# Revit family: DA_Клапан_Регулятор_Расхода_КРП_VEOX
name_source: partatom
category: Арматура воздуховодов
units: mm (PartAtom-declared; Revit-internal decimal feet)

## family parameters
Всегда вертикально = Нет
На основе рабочей плоскости = Нет
Номер OmniClass = 23.33.41.17.13
Общий = Нет
При загрузке вырезать с полостями = Нет
Размер круглого соединителя = Использовать диаметр
Тип детали = Вставляется

## types (2) — shared parameters
ADSK_Дата изменения = 13.01.2023
ADSK_Единица измерения = шт.
ADSK_Завод-изготовитель = Veox
ADSK_Количество = 1
ADSK_Марка = КРП
ADSK_Наименование краткое = клапан
CSV = ПР
URL = https://veox.ru
s = 4 мм
КМС = 6.5
Корпус = Оцинкованная сталь
Лопатка = Оцинкованная сталь
Максимальный размер клапана = 600мм
Минимальный размер клапана = 150мм
Фланец = Оцинкованная сталь
Хомут быстросъемный = Да
вылет x2 = 50 мм
тип = 2
zero-valued in all types: Отметка по умолчанию

## per-type parameters (varying)
| type | ИЗОЛЯЦИЯ | Регулятор | сдвиг изоляции |
| КРП  (без изоляции) | Нет | регулятор : 70 | 2 мм |
| КРП  (c изоляцией) | Да | регулятор : 100 | 50 мм |

## geometry (parser evidence)
native form markers: Sweep x2
no freeform markers — native parametric forms only
